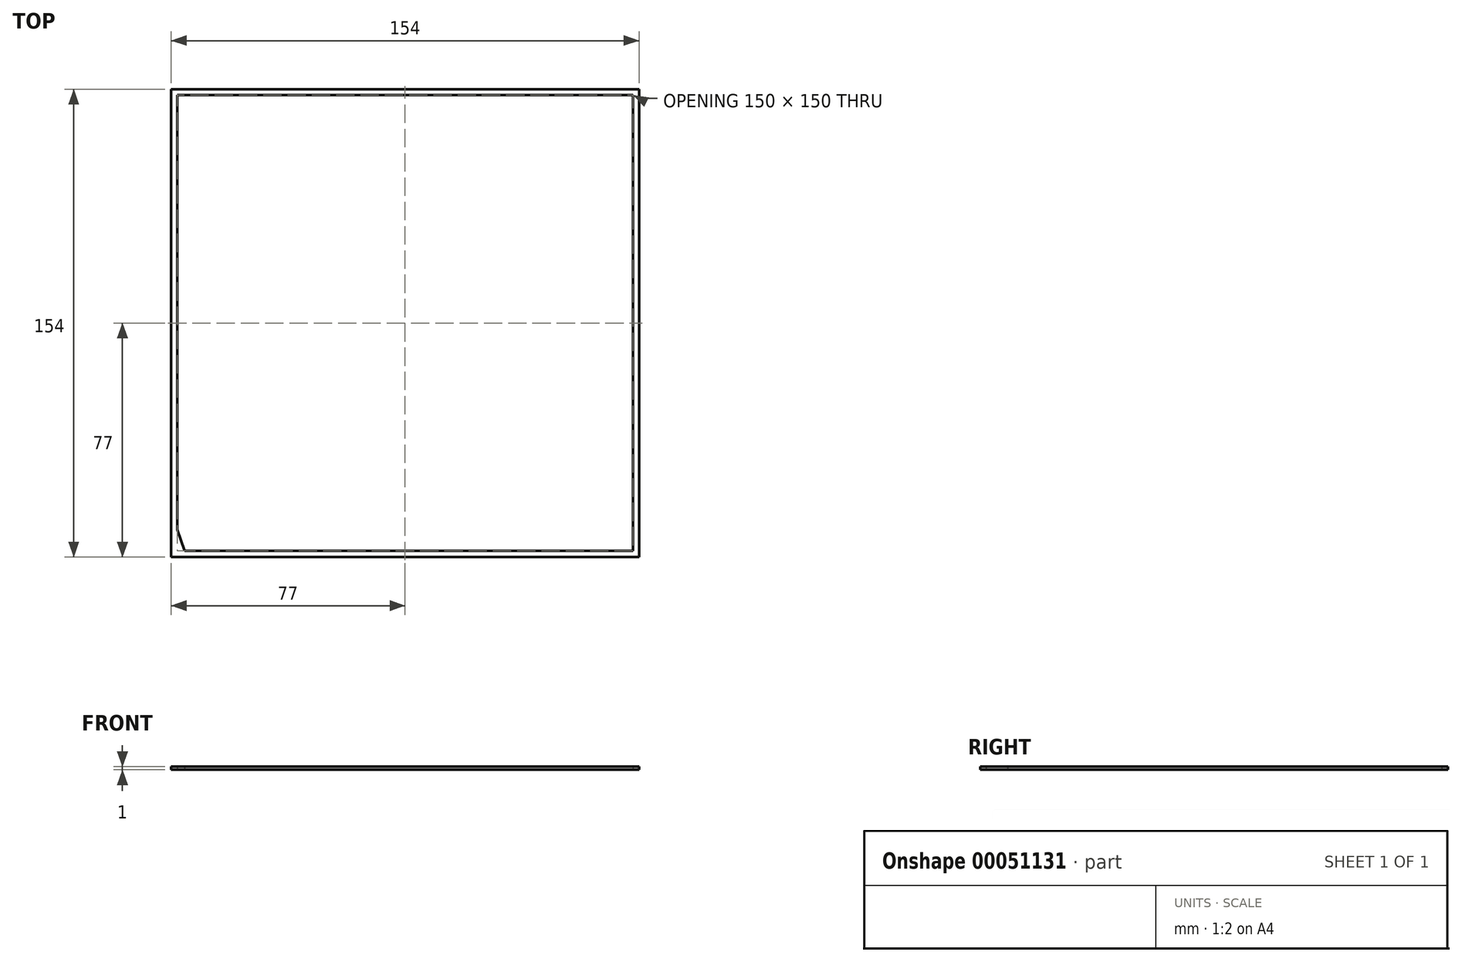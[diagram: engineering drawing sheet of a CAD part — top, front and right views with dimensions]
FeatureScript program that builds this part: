
annotation { "Feature Type Name" : "Feature", "Feature Type Description" : "" }
export const myFeature = defineFeature(function(context is Context, id is Id, definition is map)
    precondition{}
    {
        {
            var Q0;
            Q0=qCreatedBy(makeId("Top.planeOp"),FACE);
            var sketch = newSketch(context, id + "F0", { "sketchPlane" : qUnion([Q0])});
            skLineSegment(sketch, "E0.bottom", {"start": v(0, 0) * mm, "end": v(150, 0) * mm});
            skLineSegment(sketch, "E0.top", {"start": v(0, 150) * mm, "end": v(150, 150) * mm});
            skLineSegment(sketch, "E0.left", {"start": v(0, 0) * mm, "end": v(0, 150) * mm});
            skLineSegment(sketch, "E0.right", {"start": v(150, 0) * mm, "end": v(150, 150) * mm});
            skLineSegment(sketch, "E1.0", {"start": v(-2, -2) * mm, "end": v(-2, 152) * mm});
            skLineSegment(sketch, "E1.1", {"start": v(-2, -2) * mm, "end": v(152, -2) * mm});
            skLineSegment(sketch, "E1.2", {"start": v(152, -2) * mm, "end": v(152, 152) * mm});
            skLineSegment(sketch, "E1.3", {"start": v(-2, 152) * mm, "end": v(152, 152) * mm});
            skLineSegment(sketch, "E2", {"start": v(0, 7.07) * mm, "end": v(2.4, 0) * mm});
            skSolve(sketch);
        }
        {
            var Q0;
            Q0 = qSketchRegion(id + "F0", true);
            var Q1;
            {var subQ0=sQuery(id+"F0.wireOp",EDGE,"e3ec3646-0e03-48ac-9754-db47828aa7af");var subQ1=sQuery(id+"F0.wireOp",EDGE,"E0.left");var subQ2=makeQuery(id+"F0.imprint","INTERSECT",VERTEX,{"disambiguationData":[OD(0.0)],"derivedFrom":[subQ1,subQ0]});Q1=makeQuery(id+"F0.imprint","IMPRINT",FACE,{"disambiguationData":[TD([[makeQuery(id+"F0.imprint","IMPRINT",EDGE,{"disambiguationData":[TD([[subQ2,-1.0]])],"derivedFrom":subQ1}),1.0]])]});}
            var Q2;
            {var subQ3=sQuery(id+"F0.wireOp",EDGE,"E2");Q2=makeQuery(id+"F0.imprint","IMPRINT",FACE,{"disambiguationData":[TD([[makeQuery(id+"F0.imprint","IMPRINT",EDGE,{"derivedFrom":subQ3}),-1.0]])]});}
            extrude(context, id + "F1", {"entities" : qUnion([Q0, Q1, Q2]), "depth" : 1 * mm});
        }
    });
